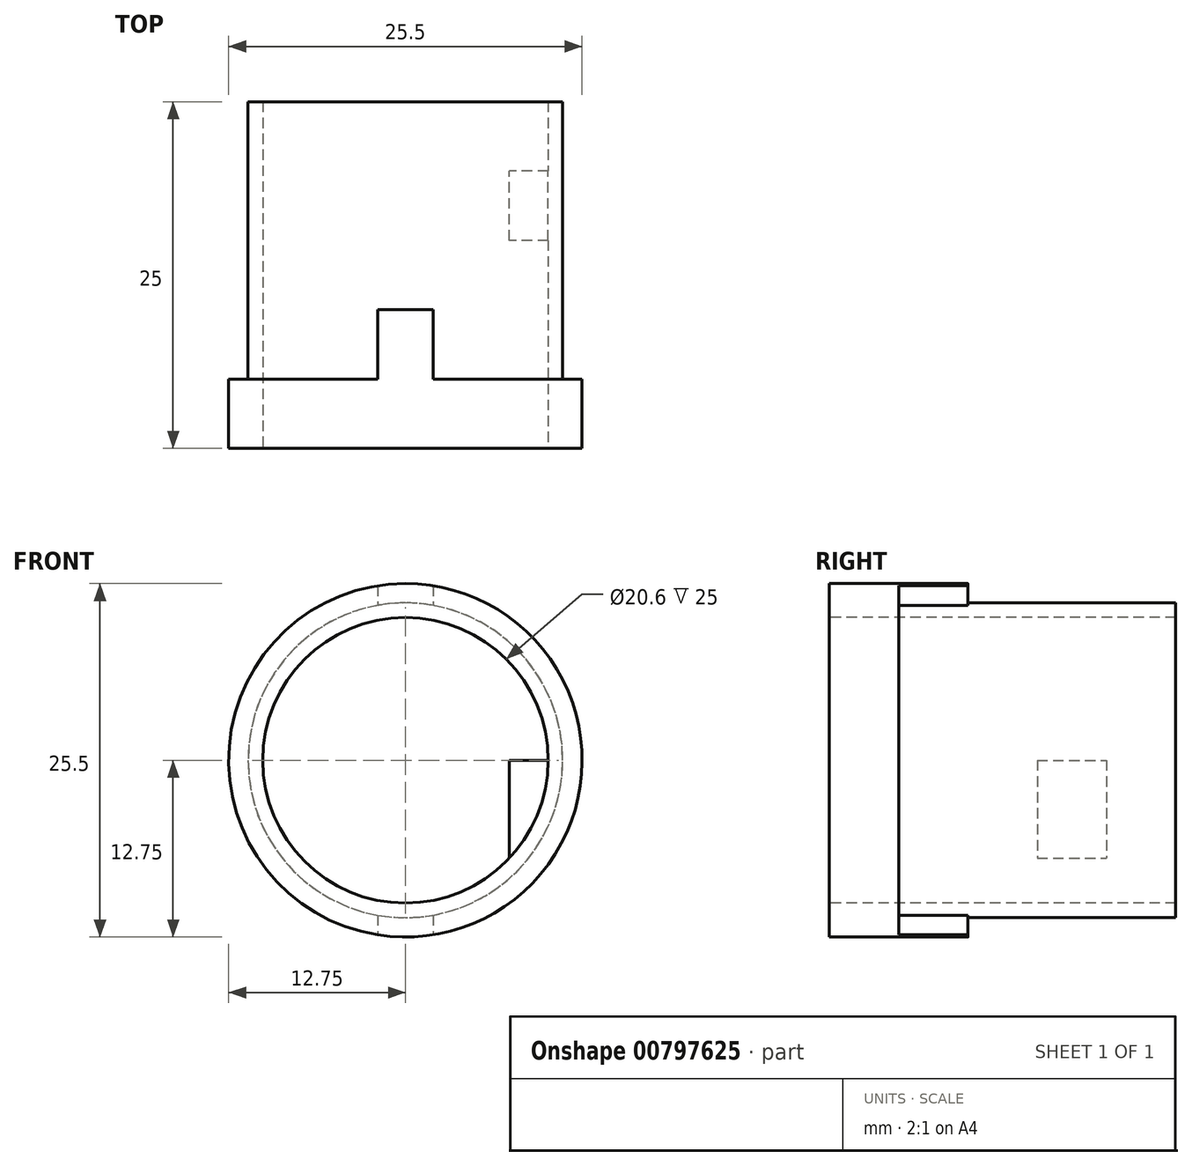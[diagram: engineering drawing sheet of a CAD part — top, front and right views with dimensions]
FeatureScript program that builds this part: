
annotation { "Feature Type Name" : "Feature", "Feature Type Description" : "" }
export const myFeature = defineFeature(function(context is Context, id is Id, definition is map)
    precondition{}
    {
        {
            var Q0;
            Q0=qCreatedBy(makeId("Front.planeOp"),FACE);
            var sketch = newSketch(context, id + "F0", { "sketchPlane" : qUnion([Q0])});
            skCircle(sketch, "E0", {"center": v(0, 0) * mm, "radius": 10.3 * mm});
            skSolve(sketch);
        }
        {
            var Q0;
            Q0=makeQuery(id+"F0.imprint","IMPRINT",FACE,{"disambiguationData":[TD([[makeQuery(id+"F0.imprint","IMPRINT",EDGE,{"derivedFrom":sQuery(id+"F0.wireOp",EDGE,"E0")}),1.0]])]});
            extrude(context, id + "F1", {"entities" : qUnion([Q0]), "depth" : 9 * mm, "offsetDistance" : 25 * mm});
        }
        {
            var Q0;
            Q0=makeQuery(id+"F1.opExtrude","CAP_FACE",FACE,{"disambiguationData":[OSD([sQuery(id+"F0.wireOp",EDGE,"E0")])],"isStart":true});
            var sketch = newSketch(context, id + "F2", { "sketchPlane" : qUnion([Q0])});
            skCircle(sketch, "E1", {"center": v(0, 0) * mm, "radius": 9.25 * mm});
            skCircle(sketch, "E2", {"center": v(0, 0) * mm, "radius": 11.25 * mm});
            skSolve(sketch);
        }
        {
            var Q0;
            Q0=makeQuery(id+"F1.opExtrude","CAP_FACE",FACE,{"disambiguationData":[OSD([sQuery(id+"F0.wireOp",EDGE,"E0")])],"isStart":false});
            var sketch = newSketch(context, id + "F3", { "sketchPlane" : qUnion([Q0])});
            skCircle(sketch, "E3", {"center": v(0, 0) * mm, "radius": 3.1 * mm});
            skSolve(sketch);
        }
        {
            var Q0;
            Q0=makeQuery(id+"F3.imprint","IMPRINT",FACE,{"disambiguationData":[TD([[makeQuery(id+"F3.imprint","IMPRINT",EDGE,{"derivedFrom":sQuery(id+"F3.wireOp",EDGE,"E3")}),1.0]])]});
            extrude(context, id + "F4", {"entities" : qUnion([Q0]), "operationType" : NewBodyOperationType.REMOVE, "endBound" : BoundingType.THROUGH_ALL, "oppositeDirection" : true, "depth" : 25 * mm, "offsetDistance" : 25 * mm});
        }
        {
            var Q0;
            Q0=makeQuery(id+"F1.opExtrude","CAP_FACE",FACE,{"disambiguationData":[OSD([sQuery(id+"F0.wireOp",EDGE,"E0")])],"isStart":false});
            var sketch = newSketch(context, id + "F5", { "sketchPlane" : qUnion([Q0])});
            skCircle(sketch, "E4", {"center": v(-4.33, 2.5) * mm, "radius": 2.5 * mm});
            skCircle(sketch, "E5", {"center": v(4.33, 2.5) * mm, "radius": 2.5 * mm});
            skCircle(sketch, "E6", {"center": v(0, -5) * mm, "radius": 2.5 * mm});
            skSolve(sketch);
        }
        {
            var Q0;
            {var subQ0=sQuery(id+"F5.wireOp",EDGE,"E4");var subQ1=makeQuery(id+"F4.boolean.opBoolean","COPY",EDGE,{"derivedFrom":makeQuery(id+"F4.opExtrude","CAP_EDGE",EDGE,{"disambiguationData":[OSD([sQuery(id+"F3.wireOp",EDGE,"E3")])],"isStart":true})});var subQ2=makeQuery(id+"F5.imprint","INTERSECT",VERTEX,{"disambiguationData":[OD(0.0)],"derivedFrom":[subQ1,subQ0]});Q0=makeQuery(id+"F5.imprint","IMPRINT",FACE,{"disambiguationData":[TD([[makeQuery(id+"F5.imprint","IMPRINT",EDGE,{"disambiguationData":[TD([[subQ2,1.0]])],"derivedFrom":subQ0}),1.0]])]});}
            var Q1;
            {var subQ0=sQuery(id+"F5.wireOp",EDGE,"E5");var subQ1=makeQuery(id+"F4.boolean.opBoolean","COPY",EDGE,{"derivedFrom":makeQuery(id+"F4.opExtrude","CAP_EDGE",EDGE,{"disambiguationData":[OSD([sQuery(id+"F3.wireOp",EDGE,"E3")])],"isStart":true})});var subQ2=makeQuery(id+"F5.imprint","INTERSECT",VERTEX,{"disambiguationData":[OD(0.0)],"derivedFrom":[subQ1,subQ0]});Q1=makeQuery(id+"F5.imprint","IMPRINT",FACE,{"disambiguationData":[TD([[makeQuery(id+"F5.imprint","IMPRINT",EDGE,{"disambiguationData":[TD([[subQ2,1.0]])],"derivedFrom":subQ0}),1.0]])]});}
            var Q2;
            {var subQ0=sQuery(id+"F5.wireOp",EDGE,"E6");var subQ1=makeQuery(id+"F4.boolean.opBoolean","COPY",EDGE,{"derivedFrom":makeQuery(id+"F4.opExtrude","CAP_EDGE",EDGE,{"disambiguationData":[OSD([sQuery(id+"F3.wireOp",EDGE,"E3")])],"isStart":true})});var subQ2=makeQuery(id+"F5.imprint","INTERSECT",VERTEX,{"disambiguationData":[OD(0.0)],"derivedFrom":[subQ1,subQ0]});Q2=makeQuery(id+"F5.imprint","IMPRINT",FACE,{"disambiguationData":[TD([[makeQuery(id+"F5.imprint","IMPRINT",EDGE,{"disambiguationData":[TD([[subQ2,-1.0]])],"derivedFrom":subQ0}),1.0]])]});}
            extrude(context, id + "F6", {"entities" : qUnion([Q0, Q1, Q2]), "operationType" : NewBodyOperationType.REMOVE, "oppositeDirection" : true, "depth" : 1.8 * mm, "offsetDistance" : 25 * mm});
        }
        {
            var Q0;
            Q0=makeQuery(id+"F6.boolean.opBoolean","COPY",EDGE,{"derivedFrom":makeQuery(id+"F6.opExtrude","CAP_EDGE",EDGE,{"disambiguationData":[OSD([sQuery(id+"F5.wireOp",EDGE,"E4")])],"isStart":false})});
            var Q1;
            Q1=makeQuery(id+"F6.boolean.opBoolean","COPY",EDGE,{"derivedFrom":makeQuery(id+"F6.opExtrude","CAP_EDGE",EDGE,{"disambiguationData":[OSD([sQuery(id+"F5.wireOp",EDGE,"E5")])],"isStart":false})});
            var Q2;
            Q2=makeQuery(id+"F6.boolean.opBoolean","COPY",EDGE,{"derivedFrom":makeQuery(id+"F6.opExtrude","CAP_EDGE",EDGE,{"disambiguationData":[OSD([sQuery(id+"F5.wireOp",EDGE,"E6")])],"isStart":false})});
            fillet(context, id + "F7", {"entities" : qUnion([Q0, Q1, Q2]), "radius" : 1 * mm, "tangentPropagation" : true, "allowEdgeOverflow" : false});
        }
        {
            var Q0;
            Q0=makeQuery(id+"F2.imprint","IMPRINT",FACE,{"disambiguationData":[TD([[makeQuery(id+"F2.imprint","IMPRINT",EDGE,{"derivedFrom":sQuery(id+"F2.wireOp",EDGE,"E1")}),1.0]])]});
            cPlane(context, id + "F8", {"entities" : qUnion([Q0]), "cplaneType" : CPlaneType.OFFSET, "offset" : 0 * mm, "width" : 150 * mm, "height" : 150 * mm});
        }
        {
            var Q0;
            Q0=qCreatedBy(id+"F8.planeOp",FACE);
            var sketch = newSketch(context, id + "F9", { "sketchPlane" : qUnion([Q0])});
            skCircle(sketch, "E7", {"center": v(0, 0) * mm, "radius": 12.75 * mm});
            skSolve(sketch);
        }
        {
            var Q0;
            Q0=qSketchRegion(id+"F9",true);
            extrude(context, id + "F10", {"entities" : qUnion([Q0]), "operationType" : NewBodyOperationType.ADD, "depth" : 25 * mm, "offsetDistance" : 25 * mm});
        }
        {
            var Q0;
            Q0=makeQuery(id+"F10.opExtrude","CAP_FACE",FACE,{"disambiguationData":[OSD([sQuery(id+"F9.wireOp",EDGE,"E7")])],"isStart":false});
            var sketch = newSketch(context, id + "F11", { "sketchPlane" : qUnion([Q0])});
            skCircle(sketch, "E8", {"center": v(0, 0) * mm, "radius": 3.1 * mm});
            skSolve(sketch);
        }
        {
            var Q0;
            Q0=makeQuery(id+"F11.imprint","IMPRINT",FACE,{"disambiguationData":[TD([[makeQuery(id+"F11.imprint","IMPRINT",EDGE,{"derivedFrom":sQuery(id+"F11.wireOp",EDGE,"E8")}),1.0]])]});
            extrude(context, id + "F12", {"entities" : qUnion([Q0]), "operationType" : NewBodyOperationType.REMOVE, "endBound" : BoundingType.THROUGH_ALL, "oppositeDirection" : true, "depth" : 25 * mm, "offsetDistance" : 25 * mm});
        }
        {
            var Q0;
            Q0=makeQuery(id+"F10.opExtrude","CAP_FACE",FACE,{"disambiguationData":[OSD([sQuery(id+"F9.wireOp",EDGE,"E7")])],"isStart":false});
            var sketch = newSketch(context, id + "F13", { "sketchPlane" : qUnion([Q0])});
            skCircle(sketch, "E9", {"center": v(0, 0) * mm, "radius": 11.35 * mm});
            skSolve(sketch);
        }
        {
            var Q0;
            Q0=makeQuery(id+"F13.imprint","IMPRINT",FACE,{"disambiguationData":[TD([[makeQuery(id+"F13.imprint","IMPRINT",EDGE,{"derivedFrom":sQuery(id+"F13.wireOp",EDGE,"E9")}),-1.0]])]});
            extrude(context, id + "F14", {"entities" : qUnion([Q0]), "operationType" : NewBodyOperationType.REMOVE, "oppositeDirection" : true, "depth" : 20 * mm, "offsetDistance" : 25 * mm});
        }
        {
            var Q0;
            Q0=makeQuery(id+"F14.boolean.opBoolean","COPY",FACE,{"derivedFrom":makeQuery(id+"F14.opExtrude","CAP_FACE",FACE,{"disambiguationData":[OSD([sQuery(id+"F9.wireOp",EDGE,"E7"),sQuery(id+"F13.wireOp",EDGE,"E9")])],"isStart":false})});
            var sketch = newSketch(context, id + "F15", { "sketchPlane" : qUnion([Q0])});
            skLineSegment(sketch, "E10", {"start": v(0, 13.66) * mm, "end": v(0, -14.8) * mm, "construction": true});
            skLineSegment(sketch, "E11", {"start": v(-2, 12.6) * mm, "end": v(-2, 11.17) * mm});
            skLineSegment(sketch, "E12", {"start": v(2, 12.6) * mm, "end": v(2, 11.17) * mm});
            skLineSegment(sketch, "E13", {"start": v(-14.5, 0) * mm, "end": v(13.95, 0) * mm, "construction": true});
            skLineSegment(sketch, "E14.MirrorCS", {"start": v(-6, 12.6) * mm, "end": v(-6, 11.17) * mm});
            skLineSegment(sketch, "E15.MirrorCS", {"start": v(10.5, 0) * mm, "end": v(-17.95, 0) * mm, "construction": true});
            skLineSegment(sketch, "E16", {"start": v(-2, -11.17) * mm, "end": v(-2, -12.6) * mm});
            skLineSegment(sketch, "E17", {"start": v(2, -11.17) * mm, "end": v(2, -12.6) * mm});
            skPoint(sketch, "E18.MirrorCS.end.orphan", {"position": v(-6, 11.17) * mm});
            skPoint(sketch, "E18.MirrorCS.start.orphan", {"position": v(-6, 12.6) * mm});
            skSolve(sketch);
        }
        {
            var Q0;
            {var subQ0=sQuery(id+"F15.wireOp",EDGE,"E11");Q0=makeQuery(id+"F15.imprint","IMPRINT",FACE,{"disambiguationData":[TD([[makeQuery(id+"F15.imprint","IMPRINT",EDGE,{"derivedFrom":subQ0}),1.0]])]});}
            var Q1;
            {var subQ0=sQuery(id+"F15.wireOp",EDGE,"E16");Q1=makeQuery(id+"F15.imprint","IMPRINT",FACE,{"disambiguationData":[TD([[makeQuery(id+"F15.imprint","IMPRINT",EDGE,{"derivedFrom":subQ0}),1.0]])]});}
            extrude(context, id + "F16", {"entities" : qUnion([Q0, Q1]), "operationType" : NewBodyOperationType.ADD, "depth" : 5 * mm, "offsetDistance" : 25 * mm});
        }
        {
            var Q0;
            Q0=makeQuery(id+"F1.opExtrude","CAP_FACE",FACE,{"disambiguationData":[OSD([sQuery(id+"F0.wireOp",EDGE,"E0")])],"isStart":false});
            var sketch = newSketch(context, id + "F17", { "sketchPlane" : qUnion([Q0])});
            skCircle(sketch, "E19", {"center": v(0, 0) * mm, "radius": 10.3 * mm});
            skSolve(sketch);
        }
        {
            var Q0;
            Q0 = qSketchRegion(id + "F17", true);
            extrude(context, id + "F18", {"entities" : qUnion([Q0]), "operationType" : NewBodyOperationType.REMOVE, "endBound" : BoundingType.THROUGH_ALL, "oppositeDirection" : true, "depth" : 25 * mm, "offsetDistance" : 25 * mm});
        }
        {
            var Q0;
            Q0=makeQuery(id+"F10.opExtrude","CAP_FACE",FACE,{"disambiguationData":[OSD([sQuery(id+"F9.wireOp",EDGE,"E7")])],"isStart":false});
            var sketch = newSketch(context, id + "F19", { "sketchPlane" : qUnion([Q0])});
            skLineSegment(sketch, "E20", {"start": v(-10.3, 0) * mm, "end": v(-7.5, 0) * mm});
            skLineSegment(sketch, "E21", {"start": v(-7.5, 0) * mm, "end": v(-7.5, -7.06) * mm});
            skSolve(sketch);
        }
        {
            var Q0;
            {var subQ0=sQuery(id+"F19.wireOp",EDGE,"E20");Q0=makeQuery(id+"F19.imprint","IMPRINT",FACE,{"disambiguationData":[TD([[makeQuery(id+"F19.imprint","IMPRINT",EDGE,{"derivedFrom":subQ0}),-1.0]])]});}
            extrude(context, id + "F20", {"entities" : qUnion([Q0]), "operationType" : NewBodyOperationType.ADD, "oppositeDirection" : true, "depth" : 10 * mm, "offsetDistance" : 25 * mm, "hasSecondDirection" : true, "secondDirectionOppositeDirection" : true, "secondDirectionDepth" : 5 * mm});
        }
    });
